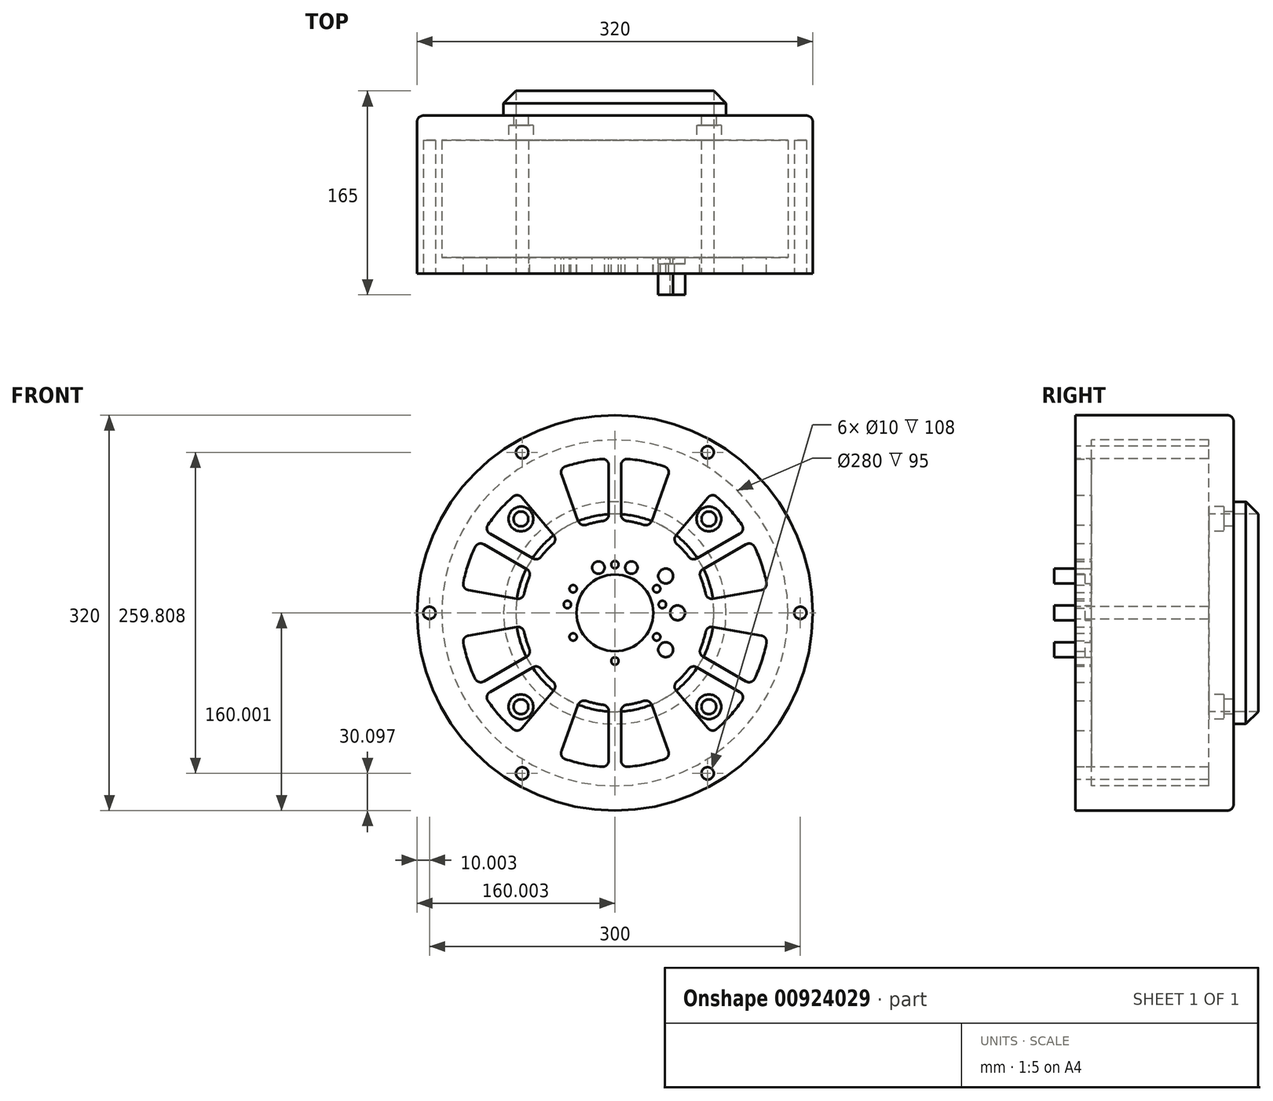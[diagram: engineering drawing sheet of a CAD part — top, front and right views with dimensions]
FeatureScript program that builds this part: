
annotation { "Feature Type Name" : "Feature", "Feature Type Description" : "" }
export const myFeature = defineFeature(function(context is Context, id is Id, definition is map)
    precondition{}
    {
        {
            var Q0;
            Q0=qCreatedBy(makeId("Front.planeOp"),FACE);
            var sketch = newSketch(context, id + "F0", { "sketchPlane" : qUnion([Q0])});
            skCircle(sketch, "E0", {"center": v(-263.66, 198.59) * mm, "radius": 134 * mm});
            skCircle(sketch, "E1", {"center": v(-263.66, 198.59) * mm, "radius": 144 * mm});
            skCircle(sketch, "E2", {"center": v(-263.66, 198.59) * mm, "radius": 150 * mm});
            skCircle(sketch, "E3", {"center": v(-188.66, 68.69) * mm, "radius": 5 * mm});
            skCircle(sketch, "E4.1.0", {"center": v(-338.66, 68.69) * mm, "radius": 5 * mm});
            skCircle(sketch, "E4.2.0", {"center": v(-413.66, 198.59) * mm, "radius": 5 * mm});
            skCircle(sketch, "E4.3.0", {"center": v(-338.66, 328.5) * mm, "radius": 5 * mm});
            skCircle(sketch, "E4.4.0", {"center": v(-188.66, 328.5) * mm, "radius": 5 * mm});
            skCircle(sketch, "E4.5.0", {"center": v(-113.66, 198.59) * mm, "radius": 5 * mm});
            skLineSegment(sketch, "E4.anchor1", {"start": v(-263.66, 198.59) * mm, "end": v(-188.66, 68.69) * mm, "construction": true});
            skLineSegment(sketch, "E4.anchor2", {"start": v(-263.66, 198.59) * mm, "end": v(-113.66, 198.59) * mm, "construction": true});
            skCircle(sketch, "E5", {"center": v(-2215.04, 1730.95) * mm, "radius": 15 * mm});
            skCircle(sketch, "E6", {"center": v(-2215.04, 1730.95) * mm, "radius": 31 * mm});
            skCircle(sketch, "E7", {"center": v(-2215.04, 1730.95) * mm, "radius": 39 * mm, "construction": true});
            skCircle(sketch, "E8", {"center": v(-2215.04, 1730.95) * mm, "radius": 62.5 * mm});
            skCircle(sketch, "E9", {"center": v(-2215.04, 1730.95) * mm, "radius": 140 * mm});
            skCircle(sketch, "E10", {"center": v(-2164.29, 1730.95) * mm, "radius": 4.86 * mm, "construction": true});
            skLineSegment(sketch, "E11", {"start": v(-2176.04, 1730.95) * mm, "end": v(-2152.54, 1730.95) * mm, "construction": true});
            skCircle(sketch, "E12", {"center": v(-2215.04, 1730.95) * mm, "radius": 50.75 * mm, "construction": true});
            skCircle(sketch, "E13.1.0", {"center": v(-2166.77, 1746.63) * mm, "radius": 4.86 * mm, "construction": true});
            skCircle(sketch, "E13.2.0", {"center": v(-2173.98, 1760.78) * mm, "radius": 4.86 * mm, "construction": true});
            skCircle(sketch, "E13.3.0", {"center": v(-2185.2, 1772) * mm, "radius": 4.86 * mm, "construction": true});
            skCircle(sketch, "E13.4.0", {"center": v(-2199.35, 1779.22) * mm, "radius": 4.86 * mm, "construction": true});
            skCircle(sketch, "E13.5.0", {"center": v(-2215.04, 1781.7) * mm, "radius": 4.86 * mm, "construction": true});
            skCircle(sketch, "E13.6.0", {"center": v(-2230.72, 1779.22) * mm, "radius": 4.86 * mm, "construction": true});
            skCircle(sketch, "E13.7.0", {"center": v(-2244.87, 1772) * mm, "radius": 4.86 * mm, "construction": true});
            skCircle(sketch, "E13.8.0", {"center": v(-2256.1, 1760.78) * mm, "radius": 4.86 * mm, "construction": true});
            skCircle(sketch, "E13.9.0", {"center": v(-2263.3, 1746.63) * mm, "radius": 4.86 * mm, "construction": true});
            skCircle(sketch, "E13.10.0", {"center": v(-2265.79, 1730.95) * mm, "radius": 4.86 * mm, "construction": true});
            skCircle(sketch, "E13.11.0", {"center": v(-2263.3, 1715.27) * mm, "radius": 4.86 * mm, "construction": true});
            skCircle(sketch, "E13.12.0", {"center": v(-2256.1, 1701.12) * mm, "radius": 4.86 * mm, "construction": true});
            skCircle(sketch, "E13.13.0", {"center": v(-2244.87, 1689.9) * mm, "radius": 4.86 * mm, "construction": true});
            skCircle(sketch, "E13.14.0", {"center": v(-2230.72, 1682.68) * mm, "radius": 4.86 * mm, "construction": true});
            skCircle(sketch, "E13.15.0", {"center": v(-2215.04, 1680.2) * mm, "radius": 4.86 * mm, "construction": true});
            skCircle(sketch, "E13.16.0", {"center": v(-2199.35, 1682.68) * mm, "radius": 4.86 * mm, "construction": true});
            skCircle(sketch, "E13.17.0", {"center": v(-2185.2, 1689.9) * mm, "radius": 4.86 * mm, "construction": true});
            skCircle(sketch, "E13.18.0", {"center": v(-2173.98, 1701.12) * mm, "radius": 4.86 * mm, "construction": true});
            skCircle(sketch, "E13.19.0", {"center": v(-2166.77, 1715.27) * mm, "radius": 4.86 * mm, "construction": true});
            skCircle(sketch, "E14", {"center": v(-2173.98, 1760.78) * mm, "radius": 6 * mm});
            skCircle(sketch, "E15", {"center": v(-2164.29, 1730.95) * mm, "radius": 6 * mm});
            skCircle(sketch, "E16", {"center": v(-2173.98, 1701.12) * mm, "radius": 6 * mm});
            skCircle(sketch, "E17", {"center": v(-2215.04, 1730.95) * mm, "radius": 165 * mm});
            skCircle(sketch, "E18", {"center": v(-2215.04, 1730.95) * mm, "radius": 160 * mm});
            skCircle(sketch, "E19", {"center": v(-2215.04, 1730.95) * mm, "radius": 150 * mm, "construction": true});
            skCircle(sketch, "E20", {"center": v(-2065.04, 1730.95) * mm, "radius": 5 * mm});
            skCircle(sketch, "E21.1.0", {"center": v(-2140.04, 1860.85) * mm, "radius": 5 * mm});
            skCircle(sketch, "E21.2.0", {"center": v(-2290.04, 1860.85) * mm, "radius": 5 * mm});
            skCircle(sketch, "E21.3.0", {"center": v(-2365.04, 1730.95) * mm, "radius": 5 * mm});
            skCircle(sketch, "E21.4.0", {"center": v(-2290.04, 1601.05) * mm, "radius": 5 * mm});
            skCircle(sketch, "E21.5.0", {"center": v(-2140.04, 1601.05) * mm, "radius": 5 * mm});
            skCircle(sketch, "E22", {"center": v(-2215.04, 1769.95) * mm, "radius": 3 * mm});
            skCircle(sketch, "E23.1.0", {"center": v(-2228.38, 1767.6) * mm, "radius": 3 * mm});
            skCircle(sketch, "E23.2.0", {"center": v(-2240.1, 1760.83) * mm, "radius": 3 * mm});
            skCircle(sketch, "E23.3.0", {"center": v(-2248.81, 1750.45) * mm, "radius": 3 * mm});
            skCircle(sketch, "E23.4.0", {"center": v(-2253.44, 1737.72) * mm, "radius": 3 * mm});
            skCircle(sketch, "E23.5.0", {"center": v(-2253.44, 1724.18) * mm, "radius": 3 * mm});
            skCircle(sketch, "E23.6.0", {"center": v(-2248.81, 1711.45) * mm, "radius": 3 * mm});
            skCircle(sketch, "E23.7.0", {"center": v(-2240.1, 1701.07) * mm, "radius": 3 * mm});
            skCircle(sketch, "E23.8.0", {"center": v(-2228.38, 1694.3) * mm, "radius": 3 * mm});
            skCircle(sketch, "E23.9.0", {"center": v(-2215.04, 1691.95) * mm, "radius": 3 * mm});
            skCircle(sketch, "E23.10.0", {"center": v(-2201.7, 1694.3) * mm, "radius": 3 * mm});
            skCircle(sketch, "E23.11.0", {"center": v(-2189.97, 1701.07) * mm, "radius": 3 * mm});
            skCircle(sketch, "E23.12.0", {"center": v(-2181.26, 1711.45) * mm, "radius": 3 * mm});
            skCircle(sketch, "E23.13.0", {"center": v(-2176.63, 1724.18) * mm, "radius": 3 * mm});
            skCircle(sketch, "E23.14.0", {"center": v(-2176.63, 1737.72) * mm, "radius": 3 * mm});
            skCircle(sketch, "E23.15.0", {"center": v(-2181.26, 1750.45) * mm, "radius": 3 * mm});
            skCircle(sketch, "E23.16.0", {"center": v(-2189.97, 1760.83) * mm, "radius": 3 * mm});
            skCircle(sketch, "E23.17.0", {"center": v(-2201.7, 1767.6) * mm, "radius": 3 * mm});
            skCircle(sketch, "E24", {"center": v(-2228.38, 1767.6) * mm, "radius": 5 * mm});
            skCircle(sketch, "E25", {"center": v(-2201.7, 1767.6) * mm, "radius": 5 * mm});
            skCircle(sketch, "E26", {"center": v(-2215.04, 1730.95) * mm, "radius": 134 * mm, "construction": true});
            skArc(sketch, "E27", {"start": v(-2174.83, 1612.6) * mm, "mid": v(-2215.04, 1855.95) * mm, "end": v(-2255.25, 1612.6) * mm, "construction": true});
            skCircle(sketch, "E28", {"center": v(-2215.04, 1730.95) * mm, "radius": 75 * mm, "construction": true});
            skLineSegment(sketch, "E29", {"start": v(-2428.79, 1730.95) * mm, "end": v(-1903.02, 1730.95) * mm, "construction": true});
            skLineSegment(sketch, "E30", {"start": v(-2290.04, 1601.05) * mm, "end": v(-2140.04, 1860.85) * mm, "construction": true});
            skLineSegment(sketch, "E31", {"start": v(-2290.04, 1860.85) * mm, "end": v(-2140.04, 1601.05) * mm, "construction": true});
            skArc(sketch, "E32", {"start": v(-2238.48, 1659.7) * mm, "mid": v(-2231.52, 1657.78) * mm, "end": v(-2224.41, 1656.54) * mm});
            skArc(sketch, "E33", {"start": v(-2255.25, 1612.6) * mm, "mid": v(-2240.54, 1608.58) * mm, "end": v(-2225.45, 1606.39) * mm});
            skLineSegment(sketch, "E34", {"start": v(-2244.74, 1656.66) * mm, "end": v(-2258.34, 1619.03) * mm});
            skLineSegment(sketch, "E35", {"start": v(-2185.33, 1656.66) * mm, "end": v(-2171.73, 1619.03) * mm});
            skLineSegment(sketch, "E36", {"start": v(-2215.04, 1605.95) * mm, "end": v(-2215.04, 1655.95) * mm, "construction": true});
            skLineSegment(sketch, "E37", {"start": v(-2210.04, 1651.58) * mm, "end": v(-2210.04, 1611.37) * mm});
            skLineSegment(sketch, "E38", {"start": v(-2220.04, 1651.58) * mm, "end": v(-2220.04, 1611.37) * mm});
            skArc(sketch, "E39.trimOffspring", {"start": v(-2205.66, 1656.54) * mm, "mid": v(-2198.55, 1657.78) * mm, "end": v(-2191.6, 1659.7) * mm});
            skArc(sketch, "E40.trimOffspring", {"start": v(-2204.62, 1606.39) * mm, "mid": v(-2189.53, 1608.58) * mm, "end": v(-2174.83, 1612.6) * mm});
            skPoint(sketch, "E41.visualSharp", {"position": v(-2170.04, 1614.33) * mm});
            skArc(sketch, "E41.filletArc", {"start": v(-2174.83, 1612.6) * mm, "mid": v(-2171.93, 1615.16) * mm, "end": v(-2171.73, 1619.03) * mm});
            skPoint(sketch, "E42.visualSharp", {"position": v(-2187.04, 1661.37) * mm});
            skArc(sketch, "E42.filletArc", {"start": v(-2185.33, 1656.66) * mm, "mid": v(-2187.85, 1659.45) * mm, "end": v(-2191.6, 1659.7) * mm});
            skPoint(sketch, "E43.visualSharp", {"position": v(-2243.04, 1661.37) * mm});
            skArc(sketch, "E43.filletArc", {"start": v(-2238.48, 1659.7) * mm, "mid": v(-2242.23, 1659.45) * mm, "end": v(-2244.74, 1656.66) * mm});
            skPoint(sketch, "E44.visualSharp", {"position": v(-2260.04, 1614.33) * mm});
            skArc(sketch, "E44.filletArc", {"start": v(-2258.34, 1619.03) * mm, "mid": v(-2258.14, 1615.16) * mm, "end": v(-2255.25, 1612.6) * mm});
            skPoint(sketch, "E45.visualSharp", {"position": v(-2220.04, 1656.12) * mm});
            skArc(sketch, "E45.filletArc", {"start": v(-2220.04, 1651.58) * mm, "mid": v(-2221.29, 1654.89) * mm, "end": v(-2224.41, 1656.54) * mm});
            skPoint(sketch, "E46.visualSharp", {"position": v(-2220.04, 1606.05) * mm});
            skArc(sketch, "E46.filletArc", {"start": v(-2225.45, 1606.39) * mm, "mid": v(-2221.65, 1607.69) * mm, "end": v(-2220.04, 1611.37) * mm});
            skPoint(sketch, "E47.visualSharp", {"position": v(-2210.04, 1606.05) * mm});
            skArc(sketch, "E47.filletArc", {"start": v(-2210.04, 1611.37) * mm, "mid": v(-2208.42, 1607.69) * mm, "end": v(-2204.62, 1606.39) * mm});
            skPoint(sketch, "E48.visualSharp", {"position": v(-2210.04, 1656.12) * mm});
            skArc(sketch, "E48.filletArc", {"start": v(-2205.66, 1656.54) * mm, "mid": v(-2208.79, 1654.89) * mm, "end": v(-2210.04, 1651.58) * mm});
            skLineSegment(sketch, "E49.1.0", {"start": v(-342.04, -2720.88) * mm, "end": v(-316.25, -2690.3) * mm});
            skArc(sketch, "E49.1.1", {"start": v(-342.04, -2720.88) * mm, "mid": v(-343.2, -2724.46) * mm, "end": v(-341.55, -2727.83) * mm});
            skArc(sketch, "E49.1.2", {"start": v(-331.77, -2738.43) * mm, "mid": v(-336.4, -2732.9) * mm, "end": v(-341.55, -2727.83) * mm});
            skArc(sketch, "E49.1.3", {"start": v(-331.77, -2738.43) * mm, "mid": v(-328.78, -2740.3) * mm, "end": v(-325.3, -2739.74) * mm});
            skLineSegment(sketch, "E49.1.4", {"start": v(-325.3, -2739.74) * mm, "end": v(-290.47, -2719.63) * mm});
            skArc(sketch, "E49.1.5", {"start": v(-290.47, -2719.63) * mm, "mid": v(-288.09, -2716.4) * mm, "end": v(-288.86, -2712.45) * mm});
            skArc(sketch, "E49.1.6", {"start": v(-309.13, -2689.75) * mm, "mid": v(-312.8, -2688.53) * mm, "end": v(-316.25, -2690.3) * mm});
            skLineSegment(sketch, "E49.2.0", {"start": v(2527.37, 1064.22) * mm, "end": v(2487.99, 1071.26) * mm});
            skArc(sketch, "E49.2.1", {"start": v(2527.37, 1064.22) * mm, "mid": v(2531.05, 1065) * mm, "end": v(2533.15, 1068.13) * mm});
            skArc(sketch, "E49.2.2", {"start": v(2537.44, 1081.89) * mm, "mid": v(2534.96, 1075.11) * mm, "end": v(2533.15, 1068.13) * mm});
            skArc(sketch, "E49.2.3", {"start": v(2537.44, 1081.89) * mm, "mid": v(2537.57, 1085.42) * mm, "end": v(2535.33, 1088.16) * mm});
            skLineSegment(sketch, "E49.2.4", {"start": v(2535.33, 1088.16) * mm, "end": v(2500.5, 1108.26) * mm});
            skArc(sketch, "E49.2.5", {"start": v(2500.5, 1108.26) * mm, "mid": v(2496.5, 1108.7) * mm, "end": v(2493.48, 1106.06) * mm});
            skArc(sketch, "E49.2.6", {"start": v(2483.96, 1077.16) * mm, "mid": v(2484.74, 1073.37) * mm, "end": v(2487.99, 1071.26) * mm});
            skPoint(sketch, "E49.center", {"position": v(0, 0) * mm});
            skArc(sketch, "E50.trimOffspring", {"start": v(-2225.45, 1606.39) * mm, "mid": v(-2215.04, 1605.95) * mm, "end": v(-2204.62, 1606.39) * mm, "construction": true});
            skArc(sketch, "E51.1.0", {"start": v(-2165.06, 1675.03) * mm, "mid": v(-2159.91, 1680.1) * mm, "end": v(-2155.28, 1685.63) * mm});
            skArc(sketch, "E51.1.1", {"start": v(-2145.9, 1701.86) * mm, "mid": v(-2143.43, 1708.64) * mm, "end": v(-2141.62, 1715.63) * mm});
            skArc(sketch, "E51.1.2", {"start": v(-2135.84, 1719.53) * mm, "mid": v(-2139.52, 1718.75) * mm, "end": v(-2141.62, 1715.63) * mm});
            skArc(sketch, "E51.1.3", {"start": v(-2145.9, 1701.86) * mm, "mid": v(-2146.04, 1698.33) * mm, "end": v(-2143.8, 1695.6) * mm});
            skArc(sketch, "E51.1.4", {"start": v(-2148.8, 1686.93) * mm, "mid": v(-2152.29, 1687.5) * mm, "end": v(-2155.28, 1685.63) * mm});
            skLineSegment(sketch, "E51.1.5", {"start": v(-2148.8, 1686.93) * mm, "end": v(-2113.98, 1666.83) * mm});
            skLineSegment(sketch, "E51.1.6", {"start": v(-2165.55, 1668.08) * mm, "end": v(-2139.76, 1637.49) * mm});
            skArc(sketch, "E51.1.7", {"start": v(-2165.06, 1675.03) * mm, "mid": v(-2166.71, 1671.65) * mm, "end": v(-2165.55, 1668.08) * mm});
            skArc(sketch, "E51.1.8", {"start": v(-2139.76, 1637.49) * mm, "mid": v(-2136.31, 1635.72) * mm, "end": v(-2132.64, 1636.95) * mm});
            skArc(sketch, "E51.1.9", {"start": v(-2132.64, 1636.95) * mm, "mid": v(-2121.81, 1647.68) * mm, "end": v(-2112.37, 1659.65) * mm});
            skArc(sketch, "E51.1.10", {"start": v(-2112.37, 1659.65) * mm, "mid": v(-2111.6, 1663.6) * mm, "end": v(-2113.98, 1666.83) * mm});
            skArc(sketch, "E51.1.11", {"start": v(-2108.98, 1675.49) * mm, "mid": v(-2104.98, 1675.05) * mm, "end": v(-2101.95, 1677.69) * mm});
            skLineSegment(sketch, "E51.1.12", {"start": v(-2143.8, 1695.6) * mm, "end": v(-2108.98, 1675.49) * mm});
            skArc(sketch, "E51.1.13", {"start": v(-2101.95, 1677.69) * mm, "mid": v(-2096.3, 1691.85) * mm, "end": v(-2092.43, 1706.6) * mm});
            skLineSegment(sketch, "E51.1.14", {"start": v(-2135.84, 1719.53) * mm, "end": v(-2096.46, 1712.5) * mm});
            skArc(sketch, "E51.1.15", {"start": v(-2092.43, 1706.6) * mm, "mid": v(-2093.2, 1710.39) * mm, "end": v(-2096.46, 1712.5) * mm});
            skArc(sketch, "E51.2.0", {"start": v(-2141.62, 1746.27) * mm, "mid": v(-2143.43, 1753.26) * mm, "end": v(-2145.9, 1760.04) * mm});
            skArc(sketch, "E51.2.1", {"start": v(-2155.28, 1776.28) * mm, "mid": v(-2159.91, 1781.8) * mm, "end": v(-2165.06, 1786.87) * mm});
            skArc(sketch, "E51.2.2", {"start": v(-2165.55, 1793.82) * mm, "mid": v(-2166.71, 1790.25) * mm, "end": v(-2165.06, 1786.87) * mm});
            skArc(sketch, "E51.2.3", {"start": v(-2155.28, 1776.28) * mm, "mid": v(-2152.29, 1774.4) * mm, "end": v(-2148.8, 1774.97) * mm});
            skArc(sketch, "E51.2.4", {"start": v(-2143.8, 1766.3) * mm, "mid": v(-2146.04, 1763.57) * mm, "end": v(-2145.9, 1760.04) * mm});
            skLineSegment(sketch, "E51.2.5", {"start": v(-2143.8, 1766.3) * mm, "end": v(-2108.98, 1786.41) * mm});
            skLineSegment(sketch, "E51.2.6", {"start": v(-2135.84, 1742.37) * mm, "end": v(-2096.46, 1749.41) * mm});
            skArc(sketch, "E51.2.7", {"start": v(-2141.62, 1746.27) * mm, "mid": v(-2139.52, 1743.15) * mm, "end": v(-2135.84, 1742.37) * mm});
            skArc(sketch, "E51.2.8", {"start": v(-2096.46, 1749.41) * mm, "mid": v(-2093.2, 1751.51) * mm, "end": v(-2092.43, 1755.3) * mm});
            skArc(sketch, "E51.2.9", {"start": v(-2092.43, 1755.3) * mm, "mid": v(-2096.3, 1770.05) * mm, "end": v(-2101.95, 1784.21) * mm});
            skArc(sketch, "E51.2.10", {"start": v(-2101.95, 1784.21) * mm, "mid": v(-2104.98, 1786.85) * mm, "end": v(-2108.98, 1786.41) * mm});
            skArc(sketch, "E51.2.11", {"start": v(-2113.98, 1795.07) * mm, "mid": v(-2111.6, 1798.31) * mm, "end": v(-2112.37, 1802.25) * mm});
            skLineSegment(sketch, "E51.2.12", {"start": v(-2148.8, 1774.97) * mm, "end": v(-2113.98, 1795.07) * mm});
            skArc(sketch, "E51.2.13", {"start": v(-2112.37, 1802.25) * mm, "mid": v(-2121.81, 1814.22) * mm, "end": v(-2132.64, 1824.95) * mm});
            skLineSegment(sketch, "E51.2.14", {"start": v(-2165.55, 1793.82) * mm, "end": v(-2139.76, 1824.41) * mm});
            skArc(sketch, "E51.2.15", {"start": v(-2132.64, 1824.95) * mm, "mid": v(-2136.31, 1826.18) * mm, "end": v(-2139.76, 1824.41) * mm});
            skArc(sketch, "E51.3.0", {"start": v(-2191.6, 1802.2) * mm, "mid": v(-2198.55, 1804.12) * mm, "end": v(-2205.66, 1805.36) * mm});
            skArc(sketch, "E51.3.1", {"start": v(-2224.41, 1805.36) * mm, "mid": v(-2231.52, 1804.12) * mm, "end": v(-2238.48, 1802.2) * mm});
            skArc(sketch, "E51.3.2", {"start": v(-2244.74, 1805.24) * mm, "mid": v(-2242.23, 1802.45) * mm, "end": v(-2238.48, 1802.2) * mm});
            skArc(sketch, "E51.3.3", {"start": v(-2224.41, 1805.36) * mm, "mid": v(-2221.29, 1807.02) * mm, "end": v(-2220.04, 1810.32) * mm});
            skArc(sketch, "E51.3.4", {"start": v(-2210.04, 1810.32) * mm, "mid": v(-2208.79, 1807.02) * mm, "end": v(-2205.66, 1805.36) * mm});
            skLineSegment(sketch, "E51.3.5", {"start": v(-2210.04, 1810.32) * mm, "end": v(-2210.04, 1850.53) * mm});
            skLineSegment(sketch, "E51.3.6", {"start": v(-2185.33, 1805.24) * mm, "end": v(-2171.73, 1842.87) * mm});
            skArc(sketch, "E51.3.7", {"start": v(-2191.6, 1802.2) * mm, "mid": v(-2187.85, 1802.45) * mm, "end": v(-2185.33, 1805.24) * mm});
            skArc(sketch, "E51.3.8", {"start": v(-2171.73, 1842.87) * mm, "mid": v(-2171.93, 1846.74) * mm, "end": v(-2174.83, 1849.3) * mm});
            skArc(sketch, "E51.3.9", {"start": v(-2174.83, 1849.3) * mm, "mid": v(-2189.53, 1853.32) * mm, "end": v(-2204.62, 1855.52) * mm});
            skArc(sketch, "E51.3.10", {"start": v(-2204.62, 1855.52) * mm, "mid": v(-2208.42, 1854.21) * mm, "end": v(-2210.04, 1850.53) * mm});
            skArc(sketch, "E51.3.11", {"start": v(-2220.04, 1850.53) * mm, "mid": v(-2221.65, 1854.21) * mm, "end": v(-2225.45, 1855.52) * mm});
            skLineSegment(sketch, "E51.3.12", {"start": v(-2220.04, 1810.32) * mm, "end": v(-2220.04, 1850.53) * mm});
            skArc(sketch, "E51.3.13", {"start": v(-2225.45, 1855.52) * mm, "mid": v(-2240.54, 1853.32) * mm, "end": v(-2255.25, 1849.3) * mm});
            skLineSegment(sketch, "E51.3.14", {"start": v(-2244.74, 1805.24) * mm, "end": v(-2258.34, 1842.87) * mm});
            skArc(sketch, "E51.3.15", {"start": v(-2255.25, 1849.3) * mm, "mid": v(-2258.14, 1846.74) * mm, "end": v(-2258.34, 1842.87) * mm});
            skArc(sketch, "E51.4.0", {"start": v(-2265.02, 1786.87) * mm, "mid": v(-2270.16, 1781.8) * mm, "end": v(-2274.8, 1776.28) * mm});
            skArc(sketch, "E51.4.1", {"start": v(-2284.17, 1760.04) * mm, "mid": v(-2286.64, 1753.26) * mm, "end": v(-2288.45, 1746.27) * mm});
            skArc(sketch, "E51.4.2", {"start": v(-2294.23, 1742.37) * mm, "mid": v(-2290.55, 1743.15) * mm, "end": v(-2288.45, 1746.27) * mm});
            skArc(sketch, "E51.4.3", {"start": v(-2284.17, 1760.04) * mm, "mid": v(-2284.04, 1763.57) * mm, "end": v(-2286.28, 1766.3) * mm});
            skArc(sketch, "E51.4.4", {"start": v(-2281.28, 1774.97) * mm, "mid": v(-2277.79, 1774.4) * mm, "end": v(-2274.8, 1776.28) * mm});
            skLineSegment(sketch, "E51.4.5", {"start": v(-2281.28, 1774.97) * mm, "end": v(-2316.1, 1795.07) * mm});
            skLineSegment(sketch, "E51.4.6", {"start": v(-2264.52, 1793.82) * mm, "end": v(-2290.31, 1824.41) * mm});
            skArc(sketch, "E51.4.7", {"start": v(-2265.02, 1786.87) * mm, "mid": v(-2263.36, 1790.25) * mm, "end": v(-2264.52, 1793.82) * mm});
            skArc(sketch, "E51.4.8", {"start": v(-2290.31, 1824.41) * mm, "mid": v(-2293.76, 1826.18) * mm, "end": v(-2297.43, 1824.95) * mm});
            skArc(sketch, "E51.4.9", {"start": v(-2297.43, 1824.95) * mm, "mid": v(-2308.26, 1814.22) * mm, "end": v(-2317.7, 1802.25) * mm});
            skArc(sketch, "E51.4.10", {"start": v(-2317.7, 1802.25) * mm, "mid": v(-2318.48, 1798.31) * mm, "end": v(-2316.1, 1795.07) * mm});
            skArc(sketch, "E51.4.11", {"start": v(-2321.1, 1786.41) * mm, "mid": v(-2325.1, 1786.85) * mm, "end": v(-2328.12, 1784.21) * mm});
            skLineSegment(sketch, "E51.4.12", {"start": v(-2286.28, 1766.3) * mm, "end": v(-2321.1, 1786.41) * mm});
            skArc(sketch, "E51.4.13", {"start": v(-2328.12, 1784.21) * mm, "mid": v(-2333.76, 1770.05) * mm, "end": v(-2337.64, 1755.3) * mm});
            skLineSegment(sketch, "E51.4.14", {"start": v(-2294.23, 1742.37) * mm, "end": v(-2333.62, 1749.41) * mm});
            skArc(sketch, "E51.4.15", {"start": v(-2337.64, 1755.3) * mm, "mid": v(-2336.87, 1751.51) * mm, "end": v(-2333.62, 1749.41) * mm});
            skArc(sketch, "E51.5.0", {"start": v(-2288.45, 1715.63) * mm, "mid": v(-2286.64, 1708.64) * mm, "end": v(-2284.17, 1701.86) * mm});
            skArc(sketch, "E51.5.1", {"start": v(-2274.8, 1685.63) * mm, "mid": v(-2270.16, 1680.1) * mm, "end": v(-2265.02, 1675.03) * mm});
            skArc(sketch, "E51.5.2", {"start": v(-2264.52, 1668.08) * mm, "mid": v(-2263.36, 1671.65) * mm, "end": v(-2265.02, 1675.03) * mm});
            skArc(sketch, "E51.5.3", {"start": v(-2274.8, 1685.63) * mm, "mid": v(-2277.79, 1687.5) * mm, "end": v(-2281.28, 1686.93) * mm});
            skArc(sketch, "E51.5.4", {"start": v(-2286.28, 1695.6) * mm, "mid": v(-2284.04, 1698.33) * mm, "end": v(-2284.17, 1701.86) * mm});
            skLineSegment(sketch, "E51.5.5", {"start": v(-2286.28, 1695.6) * mm, "end": v(-2321.1, 1675.49) * mm});
            skLineSegment(sketch, "E51.5.6", {"start": v(-2294.23, 1719.53) * mm, "end": v(-2333.62, 1712.5) * mm});
            skArc(sketch, "E51.5.7", {"start": v(-2288.45, 1715.63) * mm, "mid": v(-2290.55, 1718.75) * mm, "end": v(-2294.23, 1719.53) * mm});
            skArc(sketch, "E51.5.8", {"start": v(-2333.62, 1712.5) * mm, "mid": v(-2336.87, 1710.39) * mm, "end": v(-2337.64, 1706.6) * mm});
            skArc(sketch, "E51.5.9", {"start": v(-2337.64, 1706.6) * mm, "mid": v(-2333.76, 1691.85) * mm, "end": v(-2328.12, 1677.69) * mm});
            skArc(sketch, "E51.5.10", {"start": v(-2328.12, 1677.69) * mm, "mid": v(-2325.1, 1675.05) * mm, "end": v(-2321.1, 1675.49) * mm});
            skArc(sketch, "E51.5.11", {"start": v(-2316.1, 1666.83) * mm, "mid": v(-2318.48, 1663.6) * mm, "end": v(-2317.7, 1659.65) * mm});
            skLineSegment(sketch, "E51.5.12", {"start": v(-2281.28, 1686.93) * mm, "end": v(-2316.1, 1666.83) * mm});
            skArc(sketch, "E51.5.13", {"start": v(-2317.7, 1659.65) * mm, "mid": v(-2308.26, 1647.68) * mm, "end": v(-2297.43, 1636.95) * mm});
            skLineSegment(sketch, "E51.5.14", {"start": v(-2264.52, 1668.08) * mm, "end": v(-2290.31, 1637.49) * mm});
            skArc(sketch, "E51.5.15", {"start": v(-2297.43, 1636.95) * mm, "mid": v(-2293.76, 1635.72) * mm, "end": v(-2290.31, 1637.49) * mm});
            skCircle(sketch, "E52", {"center": v(-1574.21, 16.78) * mm, "radius": 134 * mm});
            skCircle(sketch, "E53", {"center": v(-1574.21, 16.78) * mm, "radius": 144 * mm});
            skCircle(sketch, "E54", {"center": v(-1574.21, 16.78) * mm, "radius": 150 * mm});
            skCircle(sketch, "E55", {"center": v(-1499.21, -113.13) * mm, "radius": 5 * mm});
            skCircle(sketch, "E56.1.0", {"center": v(-1649.21, -113.13) * mm, "radius": 5 * mm});
            skCircle(sketch, "E56.2.0", {"center": v(-1724.21, 16.78) * mm, "radius": 5 * mm});
            skCircle(sketch, "E56.3.0", {"center": v(-1649.21, 146.68) * mm, "radius": 5 * mm});
            skCircle(sketch, "E56.4.0", {"center": v(-1499.21, 146.68) * mm, "radius": 5 * mm});
            skCircle(sketch, "E56.5.0", {"center": v(-1424.21, 16.78) * mm, "radius": 5 * mm});
            skLineSegment(sketch, "E56.anchor1", {"start": v(-1574.21, 16.78) * mm, "end": v(-1499.21, -113.13) * mm, "construction": true});
            skLineSegment(sketch, "E56.anchor2", {"start": v(-1574.21, 16.78) * mm, "end": v(-1424.21, 16.78) * mm, "construction": true});
            skCircle(sketch, "E57", {"center": v(-3525.59, 1549.14) * mm, "radius": 15 * mm});
            skCircle(sketch, "E58", {"center": v(-3525.59, 1549.14) * mm, "radius": 31 * mm});
            skCircle(sketch, "E59", {"center": v(-3525.59, 1549.14) * mm, "radius": 39 * mm, "construction": true});
            skCircle(sketch, "E60", {"center": v(-3525.59, 1549.14) * mm, "radius": 62.5 * mm});
            skCircle(sketch, "E61", {"center": v(-3525.59, 1549.14) * mm, "radius": 140 * mm});
            skCircle(sketch, "E62", {"center": v(-3474.84, 1549.14) * mm, "radius": 4.86 * mm, "construction": true});
            skLineSegment(sketch, "E63", {"start": v(-3486.59, 1549.14) * mm, "end": v(-3463.09, 1549.14) * mm, "construction": true});
            skCircle(sketch, "E64", {"center": v(-3525.59, 1549.14) * mm, "radius": 50.75 * mm, "construction": true});
            skCircle(sketch, "E65.1.0", {"center": v(-3477.32, 1564.82) * mm, "radius": 4.86 * mm, "construction": true});
            skCircle(sketch, "E65.2.0", {"center": v(-3484.53, 1578.97) * mm, "radius": 4.86 * mm, "construction": true});
            skCircle(sketch, "E65.3.0", {"center": v(-3495.76, 1590.2) * mm, "radius": 4.86 * mm, "construction": true});
            skCircle(sketch, "E65.4.0", {"center": v(-3509.9, 1597.4) * mm, "radius": 4.86 * mm, "construction": true});
            skCircle(sketch, "E65.5.0", {"center": v(-3525.59, 1599.89) * mm, "radius": 4.86 * mm, "construction": true});
            skCircle(sketch, "E65.6.0", {"center": v(-3541.27, 1597.4) * mm, "radius": 4.86 * mm, "construction": true});
            skCircle(sketch, "E65.7.0", {"center": v(-3555.42, 1590.2) * mm, "radius": 4.86 * mm, "construction": true});
            skCircle(sketch, "E65.8.0", {"center": v(-3566.65, 1578.97) * mm, "radius": 4.86 * mm, "construction": true});
            skCircle(sketch, "E65.9.0", {"center": v(-3573.86, 1564.82) * mm, "radius": 4.86 * mm, "construction": true});
            skCircle(sketch, "E65.10.0", {"center": v(-3576.34, 1549.14) * mm, "radius": 4.86 * mm, "construction": true});
            skCircle(sketch, "E65.11.0", {"center": v(-3573.86, 1533.46) * mm, "radius": 4.86 * mm, "construction": true});
            skCircle(sketch, "E65.12.0", {"center": v(-3566.65, 1519.3) * mm, "radius": 4.86 * mm, "construction": true});
            skCircle(sketch, "E65.13.0", {"center": v(-3555.42, 1508.08) * mm, "radius": 4.86 * mm, "construction": true});
            skCircle(sketch, "E65.14.0", {"center": v(-3541.27, 1500.87) * mm, "radius": 4.86 * mm, "construction": true});
            skCircle(sketch, "E65.15.0", {"center": v(-3525.59, 1498.39) * mm, "radius": 4.86 * mm, "construction": true});
            skCircle(sketch, "E65.16.0", {"center": v(-3509.9, 1500.87) * mm, "radius": 4.86 * mm, "construction": true});
            skCircle(sketch, "E65.17.0", {"center": v(-3495.76, 1508.08) * mm, "radius": 4.86 * mm, "construction": true});
            skCircle(sketch, "E65.18.0", {"center": v(-3484.53, 1519.3) * mm, "radius": 4.86 * mm, "construction": true});
            skCircle(sketch, "E65.19.0", {"center": v(-3477.32, 1533.46) * mm, "radius": 4.86 * mm, "construction": true});
            skCircle(sketch, "E66", {"center": v(-3484.53, 1578.97) * mm, "radius": 6 * mm});
            skCircle(sketch, "E67", {"center": v(-3474.84, 1549.14) * mm, "radius": 6 * mm});
            skCircle(sketch, "E68", {"center": v(-3484.53, 1519.3) * mm, "radius": 6 * mm});
            skCircle(sketch, "E69", {"center": v(-3525.59, 1549.14) * mm, "radius": 165 * mm});
            skCircle(sketch, "E70", {"center": v(-3525.59, 1549.14) * mm, "radius": 160 * mm});
            skCircle(sketch, "E71", {"center": v(-3525.59, 1549.14) * mm, "radius": 150 * mm, "construction": true});
            skCircle(sketch, "E72", {"center": v(-3375.59, 1549.14) * mm, "radius": 5 * mm});
            skCircle(sketch, "E73.1.0", {"center": v(-3450.59, 1679.04) * mm, "radius": 5 * mm});
            skCircle(sketch, "E73.2.0", {"center": v(-3600.59, 1679.04) * mm, "radius": 5 * mm});
            skCircle(sketch, "E73.3.0", {"center": v(-3675.59, 1549.14) * mm, "radius": 5 * mm});
            skCircle(sketch, "E73.4.0", {"center": v(-3600.59, 1419.24) * mm, "radius": 5 * mm});
            skCircle(sketch, "E73.5.0", {"center": v(-3450.59, 1419.24) * mm, "radius": 5 * mm});
            skCircle(sketch, "E74", {"center": v(-3525.59, 1588.14) * mm, "radius": 3 * mm});
            skCircle(sketch, "E75.1.0", {"center": v(-3538.93, 1585.79) * mm, "radius": 3 * mm});
            skCircle(sketch, "E75.2.0", {"center": v(-3550.66, 1579.02) * mm, "radius": 3 * mm});
            skCircle(sketch, "E75.3.0", {"center": v(-3559.36, 1568.64) * mm, "radius": 3 * mm});
            skCircle(sketch, "E75.4.0", {"center": v(-3564, 1555.91) * mm, "radius": 3 * mm});
            skCircle(sketch, "E75.5.0", {"center": v(-3564, 1542.37) * mm, "radius": 3 * mm});
            skCircle(sketch, "E75.6.0", {"center": v(-3559.36, 1529.64) * mm, "radius": 3 * mm});
            skCircle(sketch, "E75.7.0", {"center": v(-3550.66, 1519.26) * mm, "radius": 3 * mm});
            skCircle(sketch, "E75.8.0", {"center": v(-3538.93, 1512.5) * mm, "radius": 3 * mm});
            skCircle(sketch, "E75.9.0", {"center": v(-3525.59, 1510.14) * mm, "radius": 3 * mm});
            skCircle(sketch, "E75.10.0", {"center": v(-3512.25, 1512.5) * mm, "radius": 3 * mm});
            skCircle(sketch, "E75.11.0", {"center": v(-3500.52, 1519.26) * mm, "radius": 3 * mm});
            skCircle(sketch, "E75.12.0", {"center": v(-3491.81, 1529.64) * mm, "radius": 3 * mm});
            skCircle(sketch, "E75.13.0", {"center": v(-3487.18, 1542.37) * mm, "radius": 3 * mm});
            skCircle(sketch, "E75.14.0", {"center": v(-3487.18, 1555.91) * mm, "radius": 3 * mm});
            skCircle(sketch, "E75.15.0", {"center": v(-3491.81, 1568.64) * mm, "radius": 3 * mm});
            skCircle(sketch, "E75.16.0", {"center": v(-3500.52, 1579.02) * mm, "radius": 3 * mm});
            skCircle(sketch, "E75.17.0", {"center": v(-3512.25, 1585.79) * mm, "radius": 3 * mm});
            skCircle(sketch, "E76", {"center": v(-3538.93, 1585.79) * mm, "radius": 5 * mm});
            skCircle(sketch, "E77", {"center": v(-3512.25, 1585.79) * mm, "radius": 5 * mm});
            skCircle(sketch, "E78", {"center": v(-3525.59, 1549.14) * mm, "radius": 134 * mm, "construction": true});
            skArc(sketch, "E79", {"start": v(-3485.38, 1430.78) * mm, "mid": v(-3525.59, 1674.14) * mm, "end": v(-3565.8, 1430.78) * mm, "construction": true});
            skCircle(sketch, "E80", {"center": v(-3525.59, 1549.14) * mm, "radius": 75 * mm, "construction": true});
            skLineSegment(sketch, "E81", {"start": v(-3739.34, 1549.14) * mm, "end": v(-3213.57, 1549.14) * mm, "construction": true});
            skLineSegment(sketch, "E82", {"start": v(-3600.59, 1419.24) * mm, "end": v(-3450.59, 1679.04) * mm, "construction": true});
            skLineSegment(sketch, "E83", {"start": v(-3600.59, 1679.04) * mm, "end": v(-3450.59, 1419.24) * mm, "construction": true});
            skArc(sketch, "E84", {"start": v(-3549.03, 1477.9) * mm, "mid": v(-3542.07, 1475.97) * mm, "end": v(-3534.96, 1474.73) * mm});
            skArc(sketch, "E85", {"start": v(-3565.8, 1430.78) * mm, "mid": v(-3551.1, 1426.77) * mm, "end": v(-3536, 1424.57) * mm});
            skLineSegment(sketch, "E86", {"start": v(-3555.3, 1474.85) * mm, "end": v(-3568.9, 1437.22) * mm});
            skLineSegment(sketch, "E87", {"start": v(-3495.89, 1474.85) * mm, "end": v(-3482.29, 1437.22) * mm});
            skLineSegment(sketch, "E88", {"start": v(-3525.59, 1424.14) * mm, "end": v(-3525.59, 1474.14) * mm, "construction": true});
            skLineSegment(sketch, "E89", {"start": v(-3520.59, 1469.77) * mm, "end": v(-3520.59, 1429.56) * mm});
            skLineSegment(sketch, "E90", {"start": v(-3530.59, 1469.77) * mm, "end": v(-3530.59, 1429.56) * mm});
            skArc(sketch, "E91.trimOffspring", {"start": v(-3516.21, 1474.73) * mm, "mid": v(-3509.1, 1475.97) * mm, "end": v(-3502.15, 1477.9) * mm});
            skArc(sketch, "E92.trimOffspring", {"start": v(-3515.17, 1424.57) * mm, "mid": v(-3500.09, 1426.77) * mm, "end": v(-3485.38, 1430.78) * mm});
            skPoint(sketch, "E93.visualSharp", {"position": v(-3480.59, 1432.52) * mm});
            skArc(sketch, "E93.filletArc", {"start": v(-3485.38, 1430.78) * mm, "mid": v(-3482.48, 1433.35) * mm, "end": v(-3482.29, 1437.22) * mm});
            skPoint(sketch, "E94.visualSharp", {"position": v(-3497.59, 1479.56) * mm});
            skArc(sketch, "E94.filletArc", {"start": v(-3495.89, 1474.85) * mm, "mid": v(-3498.4, 1477.64) * mm, "end": v(-3502.15, 1477.9) * mm});
            skPoint(sketch, "E95.visualSharp", {"position": v(-3553.59, 1479.56) * mm});
            skArc(sketch, "E95.filletArc", {"start": v(-3549.03, 1477.9) * mm, "mid": v(-3552.78, 1477.64) * mm, "end": v(-3555.3, 1474.85) * mm});
            skPoint(sketch, "E96.visualSharp", {"position": v(-3570.59, 1432.52) * mm});
            skArc(sketch, "E96.filletArc", {"start": v(-3568.9, 1437.22) * mm, "mid": v(-3568.7, 1433.35) * mm, "end": v(-3565.8, 1430.78) * mm});
            skPoint(sketch, "E97.visualSharp", {"position": v(-3530.59, 1474.3) * mm});
            skArc(sketch, "E97.filletArc", {"start": v(-3530.59, 1469.77) * mm, "mid": v(-3531.84, 1473.07) * mm, "end": v(-3534.96, 1474.73) * mm});
            skPoint(sketch, "E98.visualSharp", {"position": v(-3530.59, 1424.24) * mm});
            skArc(sketch, "E98.filletArc", {"start": v(-3536, 1424.57) * mm, "mid": v(-3532.2, 1425.88) * mm, "end": v(-3530.59, 1429.56) * mm});
            skPoint(sketch, "E99.visualSharp", {"position": v(-3520.59, 1424.24) * mm});
            skArc(sketch, "E99.filletArc", {"start": v(-3520.59, 1429.56) * mm, "mid": v(-3518.97, 1425.88) * mm, "end": v(-3515.17, 1424.57) * mm});
            skPoint(sketch, "E100.visualSharp", {"position": v(-3520.59, 1474.3) * mm});
            skArc(sketch, "E100.filletArc", {"start": v(-3516.21, 1474.73) * mm, "mid": v(-3519.34, 1473.07) * mm, "end": v(-3520.59, 1469.77) * mm});
            skLineSegment(sketch, "E101.1.0", {"start": v(-1652.6, -2902.7) * mm, "end": v(-1626.8, -2872.1) * mm});
            skArc(sketch, "E101.1.1", {"start": v(-1652.6, -2902.7) * mm, "mid": v(-1653.76, -2906.27) * mm, "end": v(-1652.1, -2909.64) * mm});
            skArc(sketch, "E101.1.2", {"start": v(-1642.33, -2920.24) * mm, "mid": v(-1646.96, -2914.7) * mm, "end": v(-1652.1, -2909.64) * mm});
            skArc(sketch, "E101.1.3", {"start": v(-1642.33, -2920.24) * mm, "mid": v(-1639.33, -2922.12) * mm, "end": v(-1635.84, -2921.55) * mm});
            skLineSegment(sketch, "E101.1.4", {"start": v(-1635.84, -2921.55) * mm, "end": v(-1601.02, -2901.44) * mm});
            skArc(sketch, "E101.1.5", {"start": v(-1601.02, -2901.44) * mm, "mid": v(-1598.64, -2898.2) * mm, "end": v(-1599.41, -2894.26) * mm});
            skArc(sketch, "E101.1.6", {"start": v(-1619.69, -2871.56) * mm, "mid": v(-1623.36, -2870.34) * mm, "end": v(-1626.8, -2872.1) * mm});
            skLineSegment(sketch, "E101.2.0", {"start": v(1216.82, 882.41) * mm, "end": v(1177.43, 889.45) * mm});
            skArc(sketch, "E101.2.1", {"start": v(1216.82, 882.41) * mm, "mid": v(1220.5, 883.2) * mm, "end": v(1222.6, 886.31) * mm});
            skArc(sketch, "E101.2.2", {"start": v(1226.88, 900.08) * mm, "mid": v(1224.4, 893.3) * mm, "end": v(1222.6, 886.31) * mm});
            skArc(sketch, "E101.2.3", {"start": v(1226.88, 900.08) * mm, "mid": v(1227.01, 903.61) * mm, "end": v(1224.77, 906.35) * mm});
            skLineSegment(sketch, "E101.2.4", {"start": v(1224.77, 906.35) * mm, "end": v(1189.95, 926.45) * mm});
            skArc(sketch, "E101.2.5", {"start": v(1189.95, 926.45) * mm, "mid": v(1185.96, 926.9) * mm, "end": v(1182.93, 924.25) * mm});
            skArc(sketch, "E101.2.6", {"start": v(1173.4, 895.35) * mm, "mid": v(1174.18, 891.55) * mm, "end": v(1177.43, 889.45) * mm});
            skPoint(sketch, "E101.center", {"position": v(-1310.55, -181.81) * mm});
            skArc(sketch, "E102.trimOffspring", {"start": v(-3536, 1424.57) * mm, "mid": v(-3525.59, 1424.14) * mm, "end": v(-3515.17, 1424.57) * mm, "construction": true});
            skArc(sketch, "E103.1.0", {"start": v(-3475.61, 1493.22) * mm, "mid": v(-3470.47, 1498.28) * mm, "end": v(-3465.83, 1503.81) * mm});
            skArc(sketch, "E103.1.1", {"start": v(-3456.46, 1520.05) * mm, "mid": v(-3453.98, 1526.83) * mm, "end": v(-3452.17, 1533.82) * mm});
            skArc(sketch, "E103.1.2", {"start": v(-3446.4, 1537.72) * mm, "mid": v(-3450.08, 1536.94) * mm, "end": v(-3452.17, 1533.82) * mm});
            skArc(sketch, "E103.1.3", {"start": v(-3456.46, 1520.05) * mm, "mid": v(-3456.6, 1516.52) * mm, "end": v(-3454.35, 1513.78) * mm});
            skArc(sketch, "E103.1.4", {"start": v(-3459.35, 1505.12) * mm, "mid": v(-3462.84, 1505.7) * mm, "end": v(-3465.83, 1503.81) * mm});
            skLineSegment(sketch, "E103.1.5", {"start": v(-3459.35, 1505.12) * mm, "end": v(-3424.53, 1485.02) * mm});
            skLineSegment(sketch, "E103.1.6", {"start": v(-3476.1, 1486.27) * mm, "end": v(-3450.31, 1455.68) * mm});
            skArc(sketch, "E103.1.7", {"start": v(-3475.61, 1493.22) * mm, "mid": v(-3477.27, 1489.84) * mm, "end": v(-3476.1, 1486.27) * mm});
            skArc(sketch, "E103.1.8", {"start": v(-3450.31, 1455.68) * mm, "mid": v(-3446.87, 1453.91) * mm, "end": v(-3443.2, 1455.14) * mm});
            skArc(sketch, "E103.1.9", {"start": v(-3443.2, 1455.14) * mm, "mid": v(-3432.36, 1465.87) * mm, "end": v(-3422.92, 1477.84) * mm});
            skArc(sketch, "E103.1.10", {"start": v(-3422.92, 1477.84) * mm, "mid": v(-3422.15, 1481.78) * mm, "end": v(-3424.53, 1485.02) * mm});
            skArc(sketch, "E103.1.11", {"start": v(-3419.53, 1493.68) * mm, "mid": v(-3415.53, 1493.24) * mm, "end": v(-3412.5, 1495.88) * mm});
            skLineSegment(sketch, "E103.1.12", {"start": v(-3454.35, 1513.78) * mm, "end": v(-3419.53, 1493.68) * mm});
            skArc(sketch, "E103.1.13", {"start": v(-3412.5, 1495.88) * mm, "mid": v(-3406.86, 1510.04) * mm, "end": v(-3402.99, 1524.78) * mm});
            skLineSegment(sketch, "E103.1.14", {"start": v(-3446.4, 1537.72) * mm, "end": v(-3407.01, 1530.68) * mm});
            skArc(sketch, "E103.1.15", {"start": v(-3402.99, 1524.78) * mm, "mid": v(-3403.76, 1528.58) * mm, "end": v(-3407.01, 1530.68) * mm});
            skArc(sketch, "E103.2.0", {"start": v(-3452.17, 1564.46) * mm, "mid": v(-3453.98, 1571.45) * mm, "end": v(-3456.46, 1578.23) * mm});
            skArc(sketch, "E103.2.1", {"start": v(-3465.83, 1594.46) * mm, "mid": v(-3470.47, 1600) * mm, "end": v(-3475.61, 1605.06) * mm});
            skArc(sketch, "E103.2.2", {"start": v(-3476.1, 1612.01) * mm, "mid": v(-3477.27, 1608.44) * mm, "end": v(-3475.61, 1605.06) * mm});
            skArc(sketch, "E103.2.3", {"start": v(-3465.83, 1594.46) * mm, "mid": v(-3462.84, 1592.58) * mm, "end": v(-3459.35, 1593.16) * mm});
            skArc(sketch, "E103.2.4", {"start": v(-3454.35, 1584.5) * mm, "mid": v(-3456.6, 1581.76) * mm, "end": v(-3456.46, 1578.23) * mm});
            skLineSegment(sketch, "E103.2.5", {"start": v(-3454.35, 1584.5) * mm, "end": v(-3419.53, 1604.6) * mm});
            skLineSegment(sketch, "E103.2.6", {"start": v(-3446.4, 1560.56) * mm, "end": v(-3407.01, 1567.6) * mm});
            skArc(sketch, "E103.2.7", {"start": v(-3452.17, 1564.46) * mm, "mid": v(-3450.08, 1561.34) * mm, "end": v(-3446.4, 1560.56) * mm});
            skArc(sketch, "E103.2.8", {"start": v(-3407.01, 1567.6) * mm, "mid": v(-3403.76, 1569.7) * mm, "end": v(-3402.99, 1573.5) * mm});
            skArc(sketch, "E103.2.9", {"start": v(-3402.99, 1573.5) * mm, "mid": v(-3406.86, 1588.24) * mm, "end": v(-3412.5, 1602.4) * mm});
            skArc(sketch, "E103.2.10", {"start": v(-3412.5, 1602.4) * mm, "mid": v(-3415.53, 1605.04) * mm, "end": v(-3419.53, 1604.6) * mm});
            skArc(sketch, "E103.2.11", {"start": v(-3424.53, 1613.26) * mm, "mid": v(-3422.15, 1616.5) * mm, "end": v(-3422.92, 1620.44) * mm});
            skLineSegment(sketch, "E103.2.12", {"start": v(-3459.35, 1593.16) * mm, "end": v(-3424.53, 1613.26) * mm});
            skArc(sketch, "E103.2.13", {"start": v(-3422.92, 1620.44) * mm, "mid": v(-3432.36, 1632.41) * mm, "end": v(-3443.2, 1643.14) * mm});
            skLineSegment(sketch, "E103.2.14", {"start": v(-3476.1, 1612.01) * mm, "end": v(-3450.31, 1642.6) * mm});
            skArc(sketch, "E103.2.15", {"start": v(-3443.2, 1643.14) * mm, "mid": v(-3446.87, 1644.37) * mm, "end": v(-3450.31, 1642.6) * mm});
            skArc(sketch, "E103.3.0", {"start": v(-3502.15, 1620.38) * mm, "mid": v(-3509.1, 1622.3) * mm, "end": v(-3516.21, 1623.55) * mm});
            skArc(sketch, "E103.3.1", {"start": v(-3534.96, 1623.55) * mm, "mid": v(-3542.07, 1622.3) * mm, "end": v(-3549.03, 1620.38) * mm});
            skArc(sketch, "E103.3.2", {"start": v(-3555.3, 1623.43) * mm, "mid": v(-3552.78, 1620.64) * mm, "end": v(-3549.03, 1620.38) * mm});
            skArc(sketch, "E103.3.3", {"start": v(-3534.96, 1623.55) * mm, "mid": v(-3531.84, 1625.2) * mm, "end": v(-3530.59, 1628.51) * mm});
            skArc(sketch, "E103.3.4", {"start": v(-3520.59, 1628.51) * mm, "mid": v(-3519.34, 1625.2) * mm, "end": v(-3516.21, 1623.55) * mm});
            skLineSegment(sketch, "E103.3.5", {"start": v(-3520.59, 1628.51) * mm, "end": v(-3520.59, 1668.72) * mm});
            skLineSegment(sketch, "E103.3.6", {"start": v(-3495.89, 1623.43) * mm, "end": v(-3482.29, 1661.06) * mm});
            skArc(sketch, "E103.3.7", {"start": v(-3502.15, 1620.38) * mm, "mid": v(-3498.4, 1620.64) * mm, "end": v(-3495.89, 1623.43) * mm});
            skArc(sketch, "E103.3.8", {"start": v(-3482.29, 1661.06) * mm, "mid": v(-3482.48, 1664.93) * mm, "end": v(-3485.38, 1667.5) * mm});
            skArc(sketch, "E103.3.9", {"start": v(-3485.38, 1667.5) * mm, "mid": v(-3500.09, 1671.51) * mm, "end": v(-3515.17, 1673.7) * mm});
            skArc(sketch, "E103.3.10", {"start": v(-3515.17, 1673.7) * mm, "mid": v(-3518.97, 1672.4) * mm, "end": v(-3520.59, 1668.72) * mm});
            skArc(sketch, "E103.3.11", {"start": v(-3530.59, 1668.72) * mm, "mid": v(-3532.2, 1672.4) * mm, "end": v(-3536, 1673.7) * mm});
            skLineSegment(sketch, "E103.3.12", {"start": v(-3530.59, 1628.51) * mm, "end": v(-3530.59, 1668.72) * mm});
            skArc(sketch, "E103.3.13", {"start": v(-3536, 1673.7) * mm, "mid": v(-3551.1, 1671.51) * mm, "end": v(-3565.8, 1667.5) * mm});
            skLineSegment(sketch, "E103.3.14", {"start": v(-3555.3, 1623.43) * mm, "end": v(-3568.9, 1661.06) * mm});
            skArc(sketch, "E103.3.15", {"start": v(-3565.8, 1667.5) * mm, "mid": v(-3568.7, 1664.93) * mm, "end": v(-3568.9, 1661.06) * mm});
            skArc(sketch, "E103.4.0", {"start": v(-3575.57, 1605.06) * mm, "mid": v(-3580.71, 1600) * mm, "end": v(-3585.34, 1594.46) * mm});
            skArc(sketch, "E103.4.1", {"start": v(-3594.72, 1578.23) * mm, "mid": v(-3597.2, 1571.45) * mm, "end": v(-3599, 1564.46) * mm});
            skArc(sketch, "E103.4.2", {"start": v(-3604.78, 1560.56) * mm, "mid": v(-3601.1, 1561.34) * mm, "end": v(-3599, 1564.46) * mm});
            skArc(sketch, "E103.4.3", {"start": v(-3594.72, 1578.23) * mm, "mid": v(-3594.59, 1581.76) * mm, "end": v(-3596.83, 1584.5) * mm});
            skArc(sketch, "E103.4.4", {"start": v(-3591.83, 1593.16) * mm, "mid": v(-3588.34, 1592.58) * mm, "end": v(-3585.34, 1594.46) * mm});
            skLineSegment(sketch, "E103.4.5", {"start": v(-3591.83, 1593.16) * mm, "end": v(-3626.65, 1613.26) * mm});
            skLineSegment(sketch, "E103.4.6", {"start": v(-3575.08, 1612.01) * mm, "end": v(-3600.87, 1642.6) * mm});
            skArc(sketch, "E103.4.7", {"start": v(-3575.57, 1605.06) * mm, "mid": v(-3573.91, 1608.44) * mm, "end": v(-3575.08, 1612.01) * mm});
            skArc(sketch, "E103.4.8", {"start": v(-3600.87, 1642.6) * mm, "mid": v(-3604.31, 1644.37) * mm, "end": v(-3607.98, 1643.14) * mm});
            skArc(sketch, "E103.4.9", {"start": v(-3607.98, 1643.14) * mm, "mid": v(-3618.81, 1632.41) * mm, "end": v(-3628.26, 1620.44) * mm});
            skArc(sketch, "E103.4.10", {"start": v(-3628.26, 1620.44) * mm, "mid": v(-3629.03, 1616.5) * mm, "end": v(-3626.65, 1613.26) * mm});
            skArc(sketch, "E103.4.11", {"start": v(-3631.65, 1604.6) * mm, "mid": v(-3635.65, 1605.04) * mm, "end": v(-3638.67, 1602.4) * mm});
            skLineSegment(sketch, "E103.4.12", {"start": v(-3596.83, 1584.5) * mm, "end": v(-3631.65, 1604.6) * mm});
            skArc(sketch, "E103.4.13", {"start": v(-3638.67, 1602.4) * mm, "mid": v(-3644.32, 1588.24) * mm, "end": v(-3648.2, 1573.5) * mm});
            skLineSegment(sketch, "E103.4.14", {"start": v(-3604.78, 1560.56) * mm, "end": v(-3644.17, 1567.6) * mm});
            skArc(sketch, "E103.4.15", {"start": v(-3648.2, 1573.5) * mm, "mid": v(-3647.42, 1569.7) * mm, "end": v(-3644.17, 1567.6) * mm});
            skArc(sketch, "E103.5.0", {"start": v(-3599, 1533.82) * mm, "mid": v(-3597.2, 1526.83) * mm, "end": v(-3594.72, 1520.05) * mm});
            skArc(sketch, "E103.5.1", {"start": v(-3585.34, 1503.81) * mm, "mid": v(-3580.71, 1498.28) * mm, "end": v(-3575.57, 1493.22) * mm});
            skArc(sketch, "E103.5.2", {"start": v(-3575.08, 1486.27) * mm, "mid": v(-3573.91, 1489.84) * mm, "end": v(-3575.57, 1493.22) * mm});
            skArc(sketch, "E103.5.3", {"start": v(-3585.34, 1503.81) * mm, "mid": v(-3588.34, 1505.7) * mm, "end": v(-3591.83, 1505.12) * mm});
            skArc(sketch, "E103.5.4", {"start": v(-3596.83, 1513.78) * mm, "mid": v(-3594.59, 1516.52) * mm, "end": v(-3594.72, 1520.05) * mm});
            skLineSegment(sketch, "E103.5.5", {"start": v(-3596.83, 1513.78) * mm, "end": v(-3631.65, 1493.68) * mm});
            skLineSegment(sketch, "E103.5.6", {"start": v(-3604.78, 1537.72) * mm, "end": v(-3644.17, 1530.68) * mm});
            skArc(sketch, "E103.5.7", {"start": v(-3599, 1533.82) * mm, "mid": v(-3601.1, 1536.94) * mm, "end": v(-3604.78, 1537.72) * mm});
            skArc(sketch, "E103.5.8", {"start": v(-3644.17, 1530.68) * mm, "mid": v(-3647.42, 1528.58) * mm, "end": v(-3648.2, 1524.78) * mm});
            skArc(sketch, "E103.5.9", {"start": v(-3648.2, 1524.78) * mm, "mid": v(-3644.32, 1510.04) * mm, "end": v(-3638.67, 1495.88) * mm});
            skArc(sketch, "E103.5.10", {"start": v(-3638.67, 1495.88) * mm, "mid": v(-3635.65, 1493.24) * mm, "end": v(-3631.65, 1493.68) * mm});
            skArc(sketch, "E103.5.11", {"start": v(-3626.65, 1485.02) * mm, "mid": v(-3629.03, 1481.78) * mm, "end": v(-3628.26, 1477.84) * mm});
            skLineSegment(sketch, "E103.5.12", {"start": v(-3591.83, 1505.12) * mm, "end": v(-3626.65, 1485.02) * mm});
            skArc(sketch, "E103.5.13", {"start": v(-3628.26, 1477.84) * mm, "mid": v(-3618.81, 1465.87) * mm, "end": v(-3607.98, 1455.14) * mm});
            skLineSegment(sketch, "E103.5.14", {"start": v(-3575.08, 1486.27) * mm, "end": v(-3600.87, 1455.68) * mm});
            skArc(sketch, "E103.5.15", {"start": v(-3607.98, 1455.14) * mm, "mid": v(-3604.31, 1453.91) * mm, "end": v(-3600.87, 1455.68) * mm});
            skSolve(sketch);
        }
        {
            var Q0;
            Q0=makeQuery(id+"F0.imprint","IMPRINT",FACE,{"disambiguationData":[TD([[makeQuery(id+"F0.imprint","IMPRINT",EDGE,{"derivedFrom":sQuery(id+"F0.wireOp",EDGE,"E15")}),1.0]])]});
            var Q1;
            Q1=makeQuery(id+"F0.imprint","IMPRINT",FACE,{"disambiguationData":[TD([[makeQuery(id+"F0.imprint","IMPRINT",EDGE,{"derivedFrom":sQuery(id+"F0.wireOp",EDGE,"E14")}),1.0]])]});
            var Q2;
            Q2=makeQuery(id+"F0.imprint","IMPRINT",FACE,{"disambiguationData":[TD([[makeQuery(id+"F0.imprint","IMPRINT",EDGE,{"derivedFrom":sQuery(id+"F0.wireOp",EDGE,"E16")}),1.0]])]});
            extrude(context, id + "F1", {"entities" : qUnion([Q0, Q1, Q2]), "depth" : 25 * mm, "offsetDistance" : 25 * mm});
        }
        {
            var Q0;
            Q0=makeQuery(id+"F0.imprint","IMPRINT",FACE,{"disambiguationData":[TD([[makeQuery(id+"F0.imprint","IMPRINT",EDGE,{"derivedFrom":sQuery(id+"F0.wireOp",EDGE,"E9")}),-1.0]])]});
            extrude(context, id + "F2", {"entities" : qUnion([Q0]), "oppositeDirection" : true, "depth" : 100 * mm, "offsetDistance" : 25 * mm});
        }
        {
            var Q0;
            Q0=makeQuery(id+"F0.imprint","IMPRINT",FACE,{"disambiguationData":[TD([[makeQuery(id+"F0.imprint","IMPRINT",EDGE,{"derivedFrom":sQuery(id+"F0.wireOp",EDGE,"E8")}),-1.0]])]});
            var Q1;
            Q1=makeQuery(id+"F0.imprint","IMPRINT",FACE,{"disambiguationData":[TD([[makeQuery(id+"F0.imprint","IMPRINT",EDGE,{"derivedFrom":sQuery(id+"F0.wireOp",EDGE,"E9")}),-1.0]])]});
            var Q2;
            Q2=makeQuery(id+"F0.imprint","IMPRINT",FACE,{"disambiguationData":[TD([[makeQuery(id+"F0.imprint","IMPRINT",EDGE,{"derivedFrom":sQuery(id+"F0.wireOp",EDGE,"E6")}),-1.0]])]});
            var Q3;
            Q3=makeQuery(id+"F0.imprint","IMPRINT",FACE,{"disambiguationData":[TD([[makeQuery(id+"F0.imprint","IMPRINT",EDGE,{"derivedFrom":sQuery(id+"F0.wireOp",EDGE,"E23.11.0")}),1.0]])]});
            var Q4;
            Q4=makeQuery(id+"F0.imprint","IMPRINT",FACE,{"disambiguationData":[TD([[makeQuery(id+"F0.imprint","IMPRINT",EDGE,{"derivedFrom":sQuery(id+"F0.wireOp",EDGE,"E23.10.0")}),1.0]])]});
            var Q5;
            Q5=makeQuery(id+"F0.imprint","IMPRINT",FACE,{"disambiguationData":[TD([[makeQuery(id+"F0.imprint","IMPRINT",EDGE,{"derivedFrom":sQuery(id+"F0.wireOp",EDGE,"E23.8.0")}),1.0]])]});
            var Q6;
            Q6=makeQuery(id+"F0.imprint","IMPRINT",FACE,{"disambiguationData":[TD([[makeQuery(id+"F0.imprint","IMPRINT",EDGE,{"derivedFrom":sQuery(id+"F0.wireOp",EDGE,"E23.7.0")}),1.0]])]});
            var Q7;
            Q7=makeQuery(id+"F0.imprint","IMPRINT",FACE,{"disambiguationData":[TD([[makeQuery(id+"F0.imprint","IMPRINT",EDGE,{"derivedFrom":sQuery(id+"F0.wireOp",EDGE,"E23.5.0")}),1.0]])]});
            var Q8;
            Q8=makeQuery(id+"F0.imprint","IMPRINT",FACE,{"disambiguationData":[TD([[makeQuery(id+"F0.imprint","IMPRINT",EDGE,{"derivedFrom":sQuery(id+"F0.wireOp",EDGE,"E23.13.0")}),1.0]])]});
            var Q9;
            Q9=makeQuery(id+"F0.imprint","IMPRINT",FACE,{"disambiguationData":[TD([[makeQuery(id+"F0.imprint","IMPRINT",EDGE,{"derivedFrom":sQuery(id+"F0.wireOp",EDGE,"E23.16.0")}),1.0]])]});
            var Q10;
            Q10=makeQuery(id+"F0.imprint","IMPRINT",FACE,{"disambiguationData":[TD([[makeQuery(id+"F0.imprint","IMPRINT",EDGE,{"derivedFrom":sQuery(id+"F0.wireOp",EDGE,"E23.2.0")}),1.0]])]});
            extrude(context, id + "F3", {"entities" : qUnion([Q0, Q1, Q2, Q3, Q4, Q5, Q6, Q7, Q8, Q9, Q10]), "depth" : 8 * mm, "offsetDistance" : 25 * mm});
        }
        {
            var Q0;
            Q0=makeQuery(id+"F2.opExtrude","CAP_FACE",FACE,{"disambiguationData":[OSD([sQuery(id+"F0.wireOp",EDGE,"E9"),sQuery(id+"F0.wireOp",EDGE,"E18"),sQuery(id+"F0.wireOp",EDGE,"E21.1.0"),sQuery(id+"F0.wireOp",EDGE,"E21.2.0"),sQuery(id+"F0.wireOp",EDGE,"E21.4.0"),sQuery(id+"F0.wireOp",EDGE,"E21.5.0")])],"isStart":false});
            var sketch = newSketch(context, id + "F4", { "sketchPlane" : qUnion([Q0])});
            skCircle(sketch, "E104", {"center": v(2215.04, 1730.95) * mm, "radius": 160 * mm});
            skCircle(sketch, "E105", {"center": v(2215.04, 1730.95) * mm, "radius": 90 * mm});
            skCircle(sketch, "E106", {"center": v(2215.04, 1730.95) * mm, "radius": 80 * mm});
            skCircle(sketch, "E107", {"center": v(2215.04, 1730.95) * mm, "radius": 107.5 * mm, "construction": true});
            skCircle(sketch, "E108", {"center": v(2215.04, 1623.45) * mm, "radius": 6 * mm});
            skCircle(sketch, "E109.1.0", {"center": v(2291.05, 1654.94) * mm, "radius": 6 * mm});
            skCircle(sketch, "E109.2.0", {"center": v(2322.54, 1730.95) * mm, "radius": 6 * mm});
            skCircle(sketch, "E109.3.0", {"center": v(2291.05, 1806.96) * mm, "radius": 6 * mm});
            skCircle(sketch, "E109.4.0", {"center": v(2215.04, 1838.45) * mm, "radius": 6 * mm});
            skCircle(sketch, "E109.5.0", {"center": v(2139.02, 1806.96) * mm, "radius": 6 * mm});
            skCircle(sketch, "E109.6.0", {"center": v(2107.54, 1730.95) * mm, "radius": 6 * mm});
            skCircle(sketch, "E109.7.0", {"center": v(2139.02, 1654.94) * mm, "radius": 6 * mm});
            skCircle(sketch, "E110", {"center": v(2291.05, 1806.96) * mm, "radius": 10 * mm});
            skCircle(sketch, "E111.1.0", {"center": v(2139.02, 1806.96) * mm, "radius": 10 * mm});
            skCircle(sketch, "E111.2.0", {"center": v(2139.02, 1654.94) * mm, "radius": 10 * mm});
            skCircle(sketch, "E111.3.0", {"center": v(2291.05, 1654.94) * mm, "radius": 10 * mm});
            skSolve(sketch);
        }
        {
            var Q0;
            Q0 = qSketchRegion(id + "F4", true);
            var Q1;
            Q1=makeQuery(id+"F4.imprint","IMPRINT",FACE,{"disambiguationData":[TD([[makeQuery(id+"F4.imprint","IMPRINT",EDGE,{"derivedFrom":sQuery(id+"F4.wireOp",EDGE,"E109.6.0")}),1.0]])]});
            var Q2;
            Q2=makeQuery(id+"F4.imprint","IMPRINT",FACE,{"disambiguationData":[TD([[makeQuery(id+"F4.imprint","IMPRINT",EDGE,{"derivedFrom":sQuery(id+"F4.wireOp",EDGE,"E109.4.0")}),1.0]])]});
            var Q3;
            Q3=makeQuery(id+"F4.imprint","IMPRINT",FACE,{"disambiguationData":[TD([[makeQuery(id+"F4.imprint","IMPRINT",EDGE,{"derivedFrom":sQuery(id+"F4.wireOp",EDGE,"E109.2.0")}),1.0]])]});
            var Q4;
            Q4=makeQuery(id+"F4.imprint","IMPRINT",FACE,{"disambiguationData":[TD([[makeQuery(id+"F4.imprint","IMPRINT",EDGE,{"derivedFrom":sQuery(id+"F4.wireOp",EDGE,"E108")}),1.0]])]});
            var Q5;
            Q5=makeQuery(id+"F4.imprint","IMPRINT",FACE,{"disambiguationData":[TD([[makeQuery(id+"F4.imprint","IMPRINT",EDGE,{"derivedFrom":sQuery(id+"F4.wireOp",EDGE,"E109.1.0")}),-1.0]])]});
            var Q6;
            Q6=makeQuery(id+"F4.imprint","IMPRINT",FACE,{"disambiguationData":[TD([[makeQuery(id+"F4.imprint","IMPRINT",EDGE,{"derivedFrom":sQuery(id+"F4.wireOp",EDGE,"E109.7.0")}),-1.0]])]});
            var Q7;
            Q7=makeQuery(id+"F4.imprint","IMPRINT",FACE,{"disambiguationData":[TD([[makeQuery(id+"F4.imprint","IMPRINT",EDGE,{"derivedFrom":sQuery(id+"F4.wireOp",EDGE,"E109.5.0")}),-1.0]])]});
            var Q8;
            Q8=makeQuery(id+"F4.imprint","IMPRINT",FACE,{"disambiguationData":[TD([[makeQuery(id+"F4.imprint","IMPRINT",EDGE,{"derivedFrom":sQuery(id+"F4.wireOp",EDGE,"E109.3.0")}),-1.0]])]});
            var Q9;
            Q9=makeQuery(id+"F4.imprint","IMPRINT",FACE,{"disambiguationData":[TD([[makeQuery(id+"F4.imprint","IMPRINT",EDGE,{"derivedFrom":sQuery(id+"F4.wireOp",EDGE,"E110")}),1.0]])]});
            extrude(context, id + "F5", {"entities" : qUnion([Q0, Q1, Q2, Q3, Q4, Q5, Q6, Q7, Q8, Q9]), "operationType" : NewBodyOperationType.ADD, "depth" : 20 * mm, "offsetDistance" : 25 * mm});
        }
        {
            var Q0;
            Q0=makeQuery(id+"F4.imprint","IMPRINT",FACE,{"disambiguationData":[TD([[makeQuery(id+"F4.imprint","IMPRINT",EDGE,{"derivedFrom":sQuery(id+"F4.wireOp",EDGE,"E105")}),1.0]])]});
            extrude(context, id + "F6", {"entities" : qUnion([Q0]), "operationType" : NewBodyOperationType.ADD, "depth" : 40 * mm, "offsetDistance" : 25 * mm});
        }
        {
            var Q0;
            Q0=makeQuery(id+"F6.opExtrude","CAP_EDGE",EDGE,{"disambiguationData":[OSD([sQuery(id+"F4.wireOp",EDGE,"E105")])],"isStart":false});
            chamfer(context, id + "F7", {"entities" : qUnion([Q0]), "width" : 10 * mm, "tangentPropagation" : true});
        }
        {
            var Q0;
            Q0=makeQuery(id+"F5.opExtrude","CAP_EDGE",EDGE,{"disambiguationData":[OSD([sQuery(id+"F4.wireOp",EDGE,"E104")])],"isStart":false});
            fillet(context, id + "F8", {"entities" : qUnion([Q0]), "radius" : 5 * mm, "tangentPropagation" : true, "allowEdgeOverflow" : false});
        }
        {
            var Q0;
            Q0=makeQuery(id+"F4.imprint","IMPRINT",FACE,{"disambiguationData":[TD([[makeQuery(id+"F4.imprint","IMPRINT",EDGE,{"derivedFrom":sQuery(id+"F4.wireOp",EDGE,"E109.5.0")}),-1.0]])]});
            var Q1;
            Q1=makeQuery(id+"F4.imprint","IMPRINT",FACE,{"disambiguationData":[TD([[makeQuery(id+"F4.imprint","IMPRINT",EDGE,{"derivedFrom":sQuery(id+"F4.wireOp",EDGE,"E109.7.0")}),-1.0]])]});
            var Q2;
            Q2=makeQuery(id+"F4.imprint","IMPRINT",FACE,{"disambiguationData":[TD([[makeQuery(id+"F4.imprint","IMPRINT",EDGE,{"derivedFrom":sQuery(id+"F4.wireOp",EDGE,"E110")}),1.0]])]});
            var Q3;
            Q3=makeQuery(id+"F4.imprint","IMPRINT",FACE,{"disambiguationData":[TD([[makeQuery(id+"F4.imprint","IMPRINT",EDGE,{"derivedFrom":sQuery(id+"F4.wireOp",EDGE,"E109.1.0")}),-1.0]])]});
            extrude(context, id + "F9", {"entities" : qUnion([Q0, Q1, Q2, Q3]), "operationType" : NewBodyOperationType.REMOVE, "depth" : 12 * mm, "offsetDistance" : 25 * mm});
        }
        {
            var Q0;
            Q0=makeQuery(id+"F0.imprint","IMPRINT",FACE,{"disambiguationData":[TD([[makeQuery(id+"F0.imprint","IMPRINT",EDGE,{"derivedFrom":sQuery(id+"F0.wireOp",EDGE,"E8")}),-1.0]])]});
            var Q1;
            Q1=makeQuery(id+"F0.imprint","IMPRINT",FACE,{"disambiguationData":[TD([[makeQuery(id+"F0.imprint","IMPRINT",EDGE,{"derivedFrom":sQuery(id+"F0.wireOp",EDGE,"E7")}),-1.0]])]});
            var Q2;
            Q2=makeQuery(id+"F0.imprint","IMPRINT",FACE,{"disambiguationData":[TD([[makeQuery(id+"F0.imprint","IMPRINT",EDGE,{"derivedFrom":sQuery(id+"F0.wireOp",EDGE,"E6")}),-1.0]])]});
            var Q3;
            Q3=makeQuery(id+"F0.imprint","IMPRINT",FACE,{"disambiguationData":[TD([[makeQuery(id+"F0.imprint","IMPRINT",EDGE,{"derivedFrom":sQuery(id+"F0.wireOp",EDGE,"12c8ddea-eeac-4eb7-a9d0-dcd4d7575ec5.13.0")}),1.0]])]});
            var Q4;
            Q4=makeQuery(id+"F0.imprint","IMPRINT",FACE,{"disambiguationData":[TD([[makeQuery(id+"F0.imprint","IMPRINT",EDGE,{"derivedFrom":sQuery(id+"F0.wireOp",EDGE,"12c8ddea-eeac-4eb7-a9d0-dcd4d7575ec5.16.0")}),1.0]])]});
            var Q5;
            Q5=makeQuery(id+"F0.imprint","IMPRINT",FACE,{"disambiguationData":[TD([[makeQuery(id+"F0.imprint","IMPRINT",EDGE,{"derivedFrom":sQuery(id+"F0.wireOp",EDGE,"12c8ddea-eeac-4eb7-a9d0-dcd4d7575ec5.17.0")}),1.0]])]});
            var Q6;
            Q6=makeQuery(id+"F0.imprint","IMPRINT",FACE,{"disambiguationData":[TD([[makeQuery(id+"F0.imprint","IMPRINT",EDGE,{"derivedFrom":sQuery(id+"F0.wireOp",EDGE,"12c8ddea-eeac-4eb7-a9d0-dcd4d7575ec5.1.0")}),1.0]])]});
            var Q7;
            Q7=makeQuery(id+"F0.imprint","IMPRINT",FACE,{"disambiguationData":[TD([[makeQuery(id+"F0.imprint","IMPRINT",EDGE,{"derivedFrom":sQuery(id+"F0.wireOp",EDGE,"12c8ddea-eeac-4eb7-a9d0-dcd4d7575ec5.2.0")}),1.0]])]});
            var Q8;
            Q8=makeQuery(id+"F0.imprint","IMPRINT",FACE,{"disambiguationData":[TD([[makeQuery(id+"F0.imprint","IMPRINT",EDGE,{"derivedFrom":sQuery(id+"F0.wireOp",EDGE,"12c8ddea-eeac-4eb7-a9d0-dcd4d7575ec5.5.0")}),1.0]])]});
            var Q9;
            Q9=makeQuery(id+"F0.imprint","IMPRINT",FACE,{"disambiguationData":[TD([[makeQuery(id+"F0.imprint","IMPRINT",EDGE,{"derivedFrom":sQuery(id+"F0.wireOp",EDGE,"12c8ddea-eeac-4eb7-a9d0-dcd4d7575ec5.7.0")}),1.0]])]});
            var Q10;
            Q10=makeQuery(id+"F0.imprint","IMPRINT",FACE,{"disambiguationData":[TD([[makeQuery(id+"F0.imprint","IMPRINT",EDGE,{"derivedFrom":sQuery(id+"F0.wireOp",EDGE,"12c8ddea-eeac-4eb7-a9d0-dcd4d7575ec5.8.0")}),1.0]])]});
            var Q11;
            Q11=makeQuery(id+"F0.imprint","IMPRINT",FACE,{"disambiguationData":[TD([[makeQuery(id+"F0.imprint","IMPRINT",EDGE,{"derivedFrom":sQuery(id+"F0.wireOp",EDGE,"12c8ddea-eeac-4eb7-a9d0-dcd4d7575ec5.10.0")}),1.0]])]});
            var Q12;
            Q12=makeQuery(id+"F0.imprint","IMPRINT",FACE,{"disambiguationData":[TD([[makeQuery(id+"F0.imprint","IMPRINT",EDGE,{"derivedFrom":sQuery(id+"F0.wireOp",EDGE,"12c8ddea-eeac-4eb7-a9d0-dcd4d7575ec5.11.0")}),1.0]])]});
            var Q13;
            Q13=makeQuery(id+"F0.imprint","IMPRINT",FACE,{"disambiguationData":[TD([[makeQuery(id+"F0.imprint","IMPRINT",EDGE,{"derivedFrom":sQuery(id+"F0.wireOp",EDGE,"E23.16.0")}),1.0]])]});
            var Q14;
            Q14=makeQuery(id+"F0.imprint","IMPRINT",FACE,{"disambiguationData":[TD([[makeQuery(id+"F0.imprint","IMPRINT",EDGE,{"derivedFrom":sQuery(id+"F0.wireOp",EDGE,"E23.13.0")}),1.0]])]});
            var Q15;
            Q15=makeQuery(id+"F0.imprint","IMPRINT",FACE,{"disambiguationData":[TD([[makeQuery(id+"F0.imprint","IMPRINT",EDGE,{"derivedFrom":sQuery(id+"F0.wireOp",EDGE,"E23.11.0")}),1.0]])]});
            var Q16;
            Q16=makeQuery(id+"F0.imprint","IMPRINT",FACE,{"disambiguationData":[TD([[makeQuery(id+"F0.imprint","IMPRINT",EDGE,{"derivedFrom":sQuery(id+"F0.wireOp",EDGE,"E23.10.0")}),1.0]])]});
            var Q17;
            Q17=makeQuery(id+"F0.imprint","IMPRINT",FACE,{"disambiguationData":[TD([[makeQuery(id+"F0.imprint","IMPRINT",EDGE,{"derivedFrom":sQuery(id+"F0.wireOp",EDGE,"E23.8.0")}),1.0]])]});
            var Q18;
            Q18=makeQuery(id+"F0.imprint","IMPRINT",FACE,{"disambiguationData":[TD([[makeQuery(id+"F0.imprint","IMPRINT",EDGE,{"derivedFrom":sQuery(id+"F0.wireOp",EDGE,"E23.7.0")}),1.0]])]});
            var Q19;
            Q19=makeQuery(id+"F0.imprint","IMPRINT",FACE,{"disambiguationData":[TD([[makeQuery(id+"F0.imprint","IMPRINT",EDGE,{"derivedFrom":sQuery(id+"F0.wireOp",EDGE,"E23.5.0")}),1.0]])]});
            var Q20;
            Q20=makeQuery(id+"F0.imprint","IMPRINT",FACE,{"disambiguationData":[TD([[makeQuery(id+"F0.imprint","IMPRINT",EDGE,{"derivedFrom":sQuery(id+"F0.wireOp",EDGE,"E23.2.0")}),1.0]])]});
            extrude(context, id + "F10", {"entities" : qUnion([Q0, Q1, Q2, Q3, Q4, Q5, Q6, Q7, Q8, Q9, Q10, Q11, Q12, Q13, Q14, Q15, Q16, Q17, Q18, Q19, Q20]), "operationType" : NewBodyOperationType.ADD, "oppositeDirection" : true, "depth" : 5 * mm, "offsetDistance" : 25 * mm});
        }
    });
